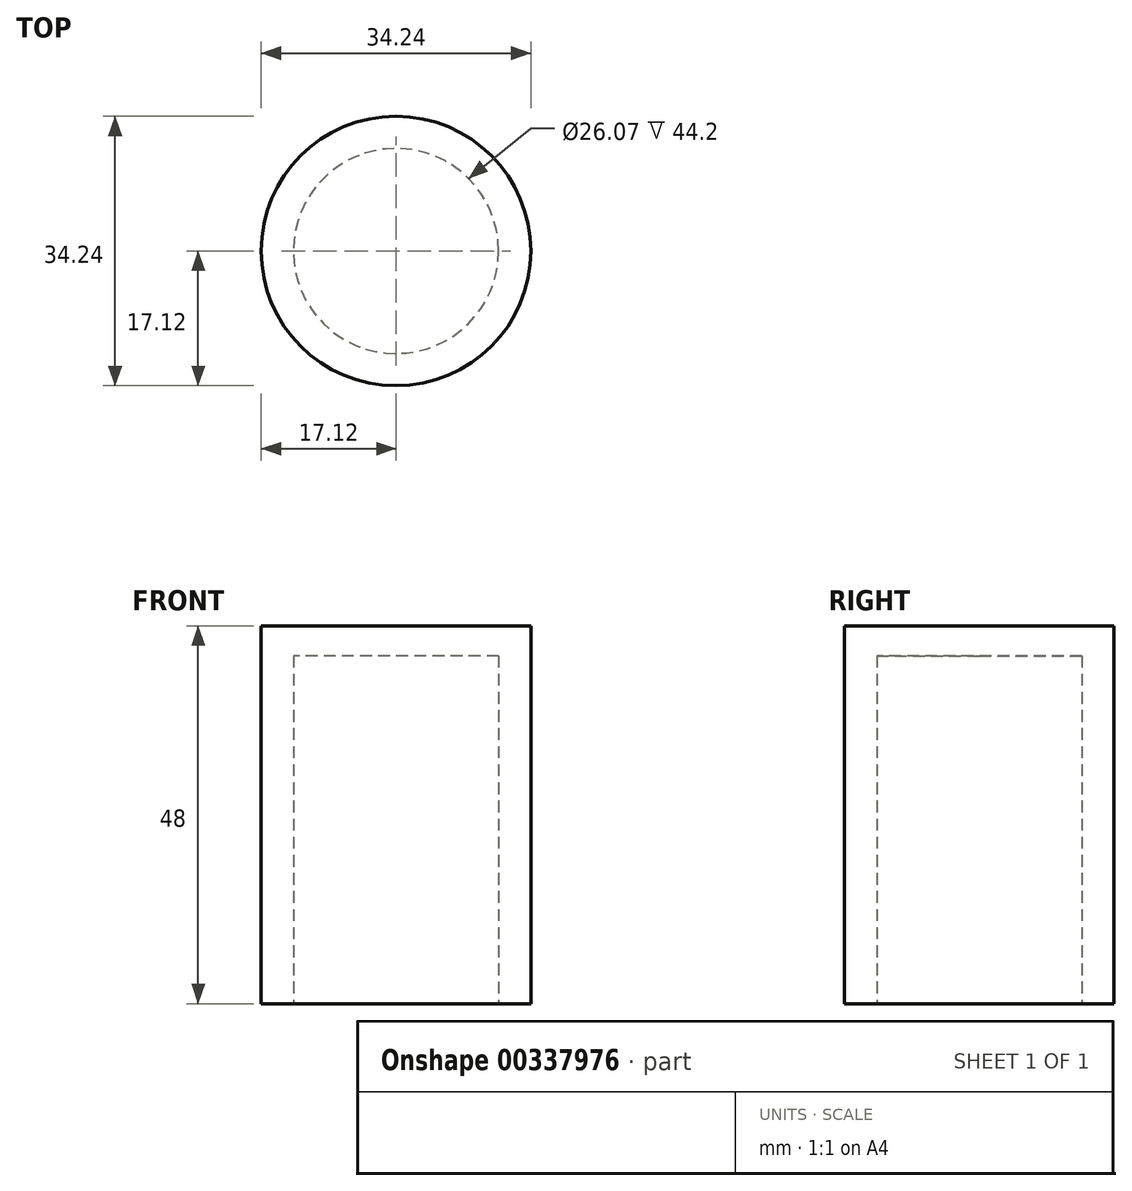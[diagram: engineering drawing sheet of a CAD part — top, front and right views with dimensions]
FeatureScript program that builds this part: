
annotation { "Feature Type Name" : "Feature", "Feature Type Description" : "" }
export const myFeature = defineFeature(function(context is Context, id is Id, definition is map)
    precondition{}
    {
        {
            var Q0;
            Q0=qCreatedBy(makeId("Top.planeOp"),FACE);
            var sketch = newSketch(context, id + "F0", { "sketchPlane" : qUnion([Q0])});
            skCircle(sketch, "E0", {"center": v(0, 0) * mm, "radius": 17.12 * mm});
            skSolve(sketch);
        }
        {
            var Q0;
            Q0=makeQuery(id+"F0.imprint","IMPRINT",FACE,{"disambiguationData":[TD([[makeQuery(id+"F0.imprint","IMPRINT",EDGE,{"derivedFrom":sQuery(id+"F0.wireOp",EDGE,"E0")}),1.0]])]});
            extrude(context, id + "F1", {"entities" : qUnion([Q0]), "depth" : 48 * mm});
        }
        {
            var Q0;
            Q0=qCreatedBy(makeId("Top.planeOp"),FACE);
            var sketch = newSketch(context, id + "F2", { "sketchPlane" : qUnion([Q0])});
            skCircle(sketch, "E1", {"center": v(0, 0) * mm, "radius": 13.03 * mm});
            skSolve(sketch);
        }
        {
            var Q0;
            Q0=makeQuery(id+"F2.imprint","IMPRINT",FACE,{"disambiguationData":[TD([[makeQuery(id+"F2.imprint","IMPRINT",EDGE,{"derivedFrom":sQuery(id+"F2.wireOp",EDGE,"E1")}),1.0]])]});
            extrude(context, id + "F3", {"entities" : qUnion([Q0]), "operationType" : NewBodyOperationType.REMOVE, "depth" : 44.2 * mm});
        }
    });
